# Revit family: Trane_TVR_Indoor_Ceiling & Floor_4TVX0012(15,18,24)EF000AA(2nd DC)
name_source: partatom
category: Equipamento mecânico
units: mm (PartAtom-declared; Revit-internal decimal feet)

## family parameters
Com base no plano de trabalho = Não
Compartilhado = Não
Corte com vazios quando carregada = Não
Cota do conector redondo = Utilizar diâmetro
Número OmniClass = 23.75.00.00
Ponto de cálculo do ambiente = Não
Sempre na vertical = Sim
Tipo de parte = Normal
Título OmniClass = Climate Control (HVAC)

## types (4) — shared parameters
Condensation = air
Depth = 660
Descrição = High efficiency air cooled
Fabricante = Trane
Gas = R410a
Gas pipe = 12.7  [stored 0.0416667 ft]
Height = 203  [stored 0.66601 ft]
Installation = Indoor installation
Liquid pipe = 6.35  [stored 0.0208333 ft]
MFA (Maximum Fuse Amps) = 15 A
Machine material = Galvanized Steel
Panel color = S1004
Power supply = 220-240V ~50/60Hz
Series = TVR ULTRA
URL = https://www.trane.com
Width = 990  [stored 3.24803 ft]

## per-type parameters (varying)
| type | Air  Flow | Cooling Capacity | Cooling Power Input | Heating Capacity | Heating Power Input | MCA (Minimum Circuit Amps) | Net Weight |
| 4TVX0012EF000AA | 650/620/595/570/550/525/500 m3/h | 4 kW | 49 W | 4 kW | 49 W | 0 A | 27.00 kg |
| 4TVX0015EF000AA | 800/750/700/650/600/550/500 m3/h | 5 kW | 115 W | 5 kW | 115 W | 1 A | 28.00 kg |
| 4TVX0018EF000AA | 800/750/700/650/600/550/500 m3/h | 6 kW | 115 W | 6 kW | 115 W | 1 A | 28.00 kg |
| 4TVX0024EF000AA | 800/750/700/650/600/550/500 m3/h | 7 kW | 115 W | 8 kW | 115 W | 1 A | 28.00 kg |

note: column(s) folded — value = type name in every type: Modelo

note: [stored X ft] marks values corroborated as IEEE doubles in the binary element streams (Revit-internal decimal feet)
